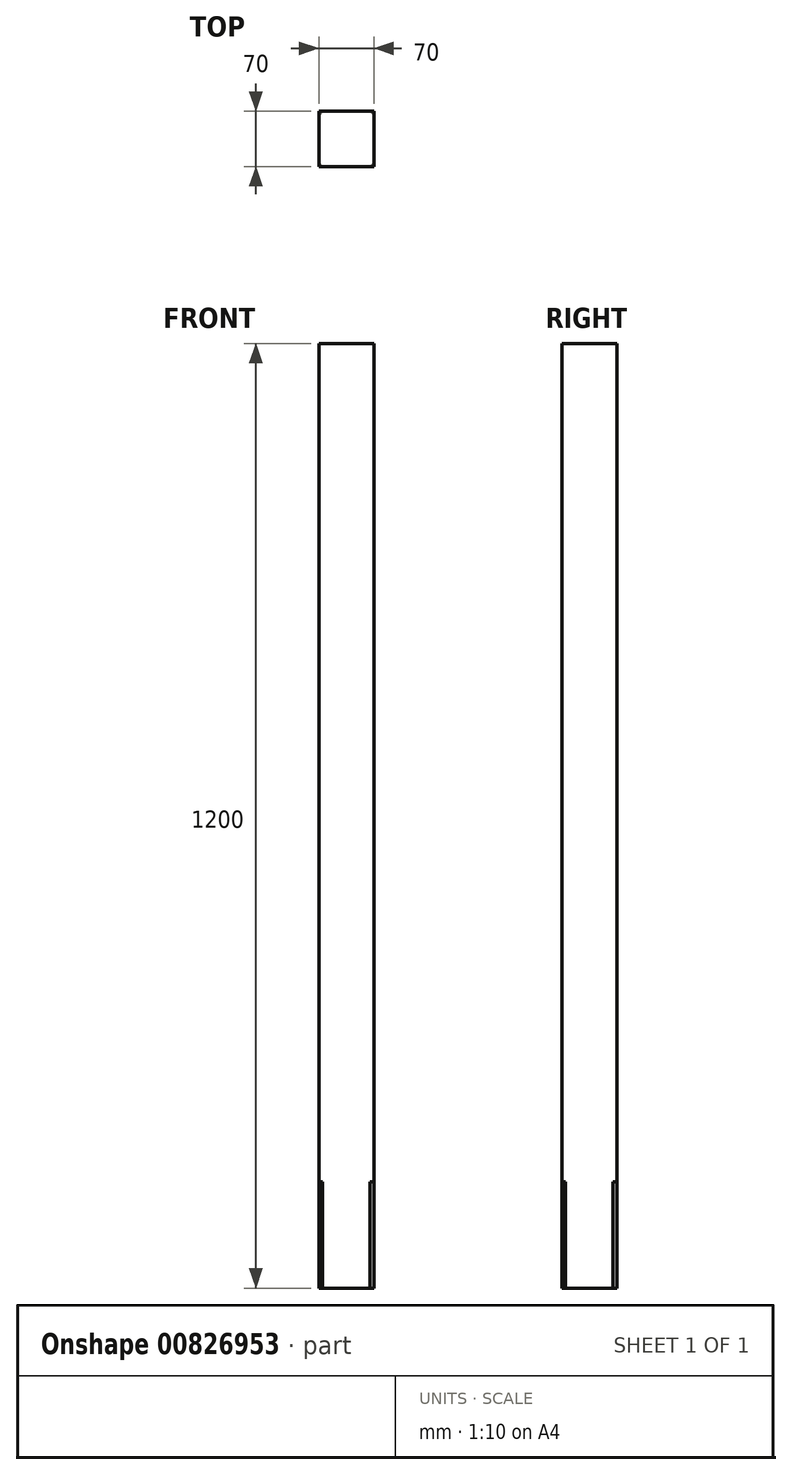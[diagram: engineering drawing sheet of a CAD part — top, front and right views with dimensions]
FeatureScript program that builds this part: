
annotation { "Feature Type Name" : "Feature", "Feature Type Description" : "" }
export const myFeature = defineFeature(function(context is Context, id is Id, definition is map)
    precondition{}
    {
        {
            var Q0;
            Q0=qCreatedBy(makeId("Top.planeOp"),FACE);
            var sketch = newSketch(context, id + "F0", { "sketchPlane" : qUnion([Q0])});
            skLineSegment(sketch, "E0.bottom", {"start": v(-35, -35) * mm, "end": v(35, -35) * mm});
            skLineSegment(sketch, "E0.top", {"start": v(-35, 35) * mm, "end": v(35, 35) * mm});
            skLineSegment(sketch, "E0.left", {"start": v(-35, -35) * mm, "end": v(-35, 35) * mm});
            skLineSegment(sketch, "E0.right", {"start": v(35, -35) * mm, "end": v(35, 35) * mm});
            skSolve(sketch);
        }
        {
            var Q0;
            Q0=makeQuery(id+"F0.imprint","IMPRINT",FACE,{"disambiguationData":[TD([[makeQuery(id+"F0.imprint","IMPRINT",EDGE,{"derivedFrom":sQuery(id+"F0.wireOp",EDGE,"E0.bottom")}),1.0]])]});
            extrude(context, id + "F1", {"entities" : qUnion([Q0]), "depth" : (150 - 15) * mm, "offsetDistance" : 25 * mm});
        }
        {
            var Q0;
            Q0=makeQuery(id+"F1.opExtrude","SWEPT_EDGE",EDGE,{"disambiguationData":[OSD([sQuery(id+"F0.wireOp",EDGE,"E0.bottom"),sQuery(id+"F0.wireOp",EDGE,"E0.right")])]});
            var Q1;
            Q1=makeQuery(id+"F1.opExtrude","SWEPT_EDGE",EDGE,{"disambiguationData":[OSD([sQuery(id+"F0.wireOp",EDGE,"E0.bottom"),sQuery(id+"F0.wireOp",EDGE,"E0.left")])]});
            var Q2;
            Q2=makeQuery(id+"F1.opExtrude","SWEPT_EDGE",EDGE,{"disambiguationData":[OSD([sQuery(id+"F0.wireOp",EDGE,"E0.top"),sQuery(id+"F0.wireOp",EDGE,"E0.right")])]});
            var Q3;
            Q3=makeQuery(id+"F1.opExtrude","SWEPT_EDGE",EDGE,{"disambiguationData":[OSD([sQuery(id+"F0.wireOp",EDGE,"E0.top"),sQuery(id+"F0.wireOp",EDGE,"E0.left")])]});
            chamfer(context, id + "F2", {"entities" : qUnion([Q0, Q1, Q2, Q3]), "width" : 5 * mm, "tangentPropagation" : true});
        }
        {
            var Q0;
            Q0=makeQuery(id+"F1.opExtrude","CAP_FACE",FACE,{"disambiguationData":[OSD([sQuery(id+"F0.wireOp",EDGE,"E0.bottom"),sQuery(id+"F0.wireOp",EDGE,"E0.top"),sQuery(id+"F0.wireOp",EDGE,"E0.left"),sQuery(id+"F0.wireOp",EDGE,"E0.right")])],"isStart":false});
            var sketch = newSketch(context, id + "F3", { "sketchPlane" : qUnion([Q0])});
            skLineSegment(sketch, "E1.bottom", {"start": v(-35, 35) * mm, "end": v(35, 35) * mm});
            skLineSegment(sketch, "E1.top", {"start": v(-35, -35) * mm, "end": v(35, -35) * mm});
            skLineSegment(sketch, "E1.left", {"start": v(-35, 35) * mm, "end": v(-35, -35) * mm});
            skLineSegment(sketch, "E1.right", {"start": v(35, 35) * mm, "end": v(35, -35) * mm});
            skSolve(sketch);
        }
        {
            var Q0;
            Q0=qSketchRegion(id+"F3",true);
            extrude(context, id + "F4", {"entities" : qUnion([Q0]), "operationType" : NewBodyOperationType.ADD, "depth" : (1200 - 150 + 15) * mm, "offsetDistance" : 25 * mm});
        }
    });
